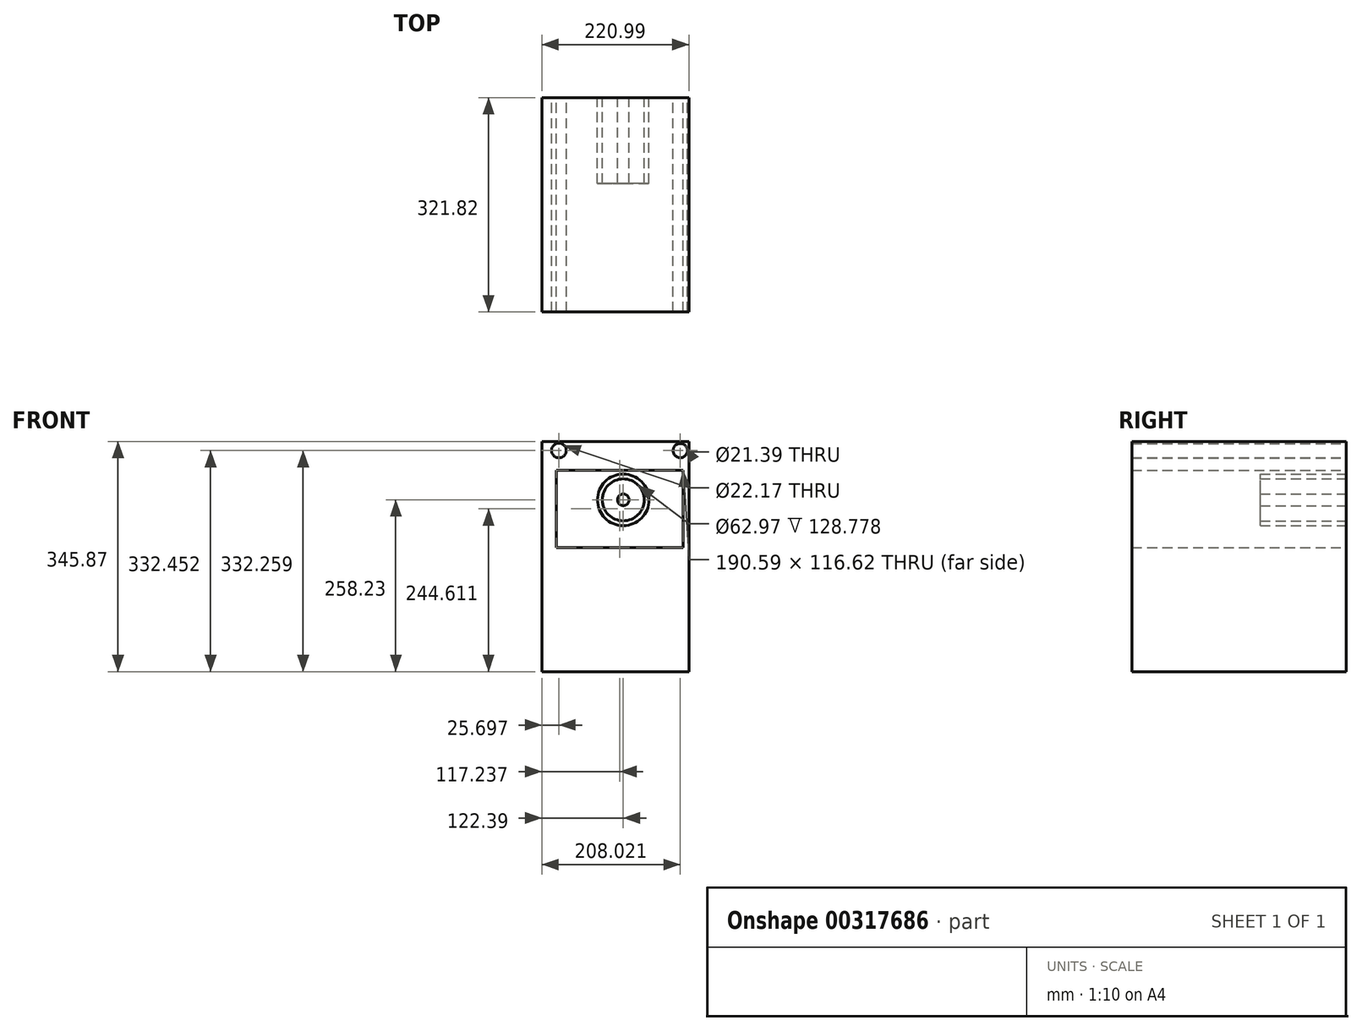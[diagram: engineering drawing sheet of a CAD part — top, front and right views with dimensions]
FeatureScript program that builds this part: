
annotation { "Feature Type Name" : "Feature", "Feature Type Description" : "" }
export const myFeature = defineFeature(function(context is Context, id is Id, definition is map)
    precondition{}
    {
        {
            var Q0;
            Q0=qCreatedBy(makeId("Front.planeOp"),FACE);
            var sketch = newSketch(context, id + "F0", { "sketchPlane" : qUnion([Q0])});
            skLineSegment(sketch, "E0.bottom", {"start": v(98.6, 50.12) * mm, "end": v(-122.4, 50.12) * mm});
            skLineSegment(sketch, "E0.top", {"start": v(98.6, -81.2) * mm, "end": v(-122.4, -81.2) * mm});
            skLineSegment(sketch, "E0.left", {"start": v(98.6, 50.12) * mm, "end": v(98.6, -81.2) * mm});
            skLineSegment(sketch, "E0.right", {"start": v(-122.4, 50.12) * mm, "end": v(-122.4, -81.2) * mm});
            skLineSegment(sketch, "E1.top", {"start": v(98.6, 87.64) * mm, "end": v(-122.4, 87.64) * mm});
            skLineSegment(sketch, "E1.left", {"start": v(98.6, 50.12) * mm, "end": v(98.6, 87.64) * mm});
            skLineSegment(sketch, "E1.right", {"start": v(-122.4, 50.12) * mm, "end": v(-122.4, 87.64) * mm});
            skCircle(sketch, "E2", {"center": v(85.63, 74.03) * mm, "radius": 10.7 * mm});
            skCircle(sketch, "E3", {"center": v(-96.7, 74.22) * mm, "radius": 11.08 * mm});
            skLineSegment(sketch, "E4.bottom", {"start": v(90.14, 44.7) * mm, "end": v(-100.45, 44.7) * mm});
            skLineSegment(sketch, "E4.top", {"start": v(90.14, -71.93) * mm, "end": v(-100.45, -71.93) * mm});
            skLineSegment(sketch, "E4.left", {"start": v(90.14, 44.7) * mm, "end": v(90.14, -71.93) * mm});
            skLineSegment(sketch, "E4.right", {"start": v(-100.45, 44.7) * mm, "end": v(-100.45, -71.93) * mm});
            skCircle(sketch, "E5", {"center": v(0, 0) * mm, "radius": 38.77 * mm});
            skCircle(sketch, "E6", {"center": v(0, 0) * mm, "radius": 8.77 * mm});
            skCircle(sketch, "E7", {"center": v(0, 0) * mm, "radius": 31.48 * mm});
            skSolve(sketch);
        }
        {
            var Q0;
            Q0 = qSketchRegion(id + "F0", true);
            var Q1;
            Q1=makeQuery(id+"F0.imprint","IMPRINT",FACE,{"disambiguationData":[TD([[makeQuery(id+"F0.imprint","IMPRINT",EDGE,{"derivedFrom":sQuery(id+"F0.wireOp",EDGE,"E5")}),1.0]])]});
            var Q2;
            Q2=makeQuery(id+"F0.imprint","IMPRINT",FACE,{"disambiguationData":[TD([[makeQuery(id+"F0.imprint","IMPRINT",EDGE,{"derivedFrom":sQuery(id+"F0.wireOp",EDGE,"E6")}),1.0]])]});
            extrude(context, id + "F1", {"entities" : qUnion([Q0, Q1, Q2]), "depth" : 128.78 * mm});
        }
        {
            var Q0;
            Q0=makeQuery(id+"F1.opExtrude","SWEPT_FACE",FACE,{"disambiguationData":[OSD([sQuery(id+"F0.wireOp",EDGE,"E0.top")])]});
            extrude(context, id + "F2", {"entities" : qUnion([Q0]), "operationType" : NewBodyOperationType.ADD, "depth" : 177.04 * mm});
        }
        {
            var Q0;
            {var subQ0=sQuery(id+"F0.wireOp",EDGE,"E0.top");Q0=makeQuery(id+"F2.boolean.opBoolean","MERGE",FACE,{"derivedFrom":[makeQuery(id+"F1.opExtrude","CAP_FACE",FACE,{"disambiguationData":[OSD([subQ0,sQuery(id+"F0.wireOp",EDGE,"E0.left"),sQuery(id+"F0.wireOp",EDGE,"E0.right"),sQuery(id+"F0.wireOp",EDGE,"E1.top"),sQuery(id+"F0.wireOp",EDGE,"E1.left"),sQuery(id+"F0.wireOp",EDGE,"E1.right"),sQuery(id+"F0.wireOp",EDGE,"E2"),sQuery(id+"F0.wireOp",EDGE,"E3"),sQuery(id+"F0.wireOp",EDGE,"E4.bottom"),sQuery(id+"F0.wireOp",EDGE,"E4.top"),sQuery(id+"F0.wireOp",EDGE,"E4.left"),sQuery(id+"F0.wireOp",EDGE,"E4.right")])],"isStart":false}),makeQuery(id+"F2.opExtrude","SWEPT_FACE",FACE,{"disambiguationData":[OSD([subQ0]),TDD([makeQuery(id+"F1.opExtrude","CAP_EDGE",EDGE,{"disambiguationData":[OSD([subQ0])],"isStart":false})])]})]});}
            extrude(context, id + "F3", {"entities" : qUnion([Q0]), "operationType" : NewBodyOperationType.ADD, "depth" : 193.04 * mm});
        }
    });
